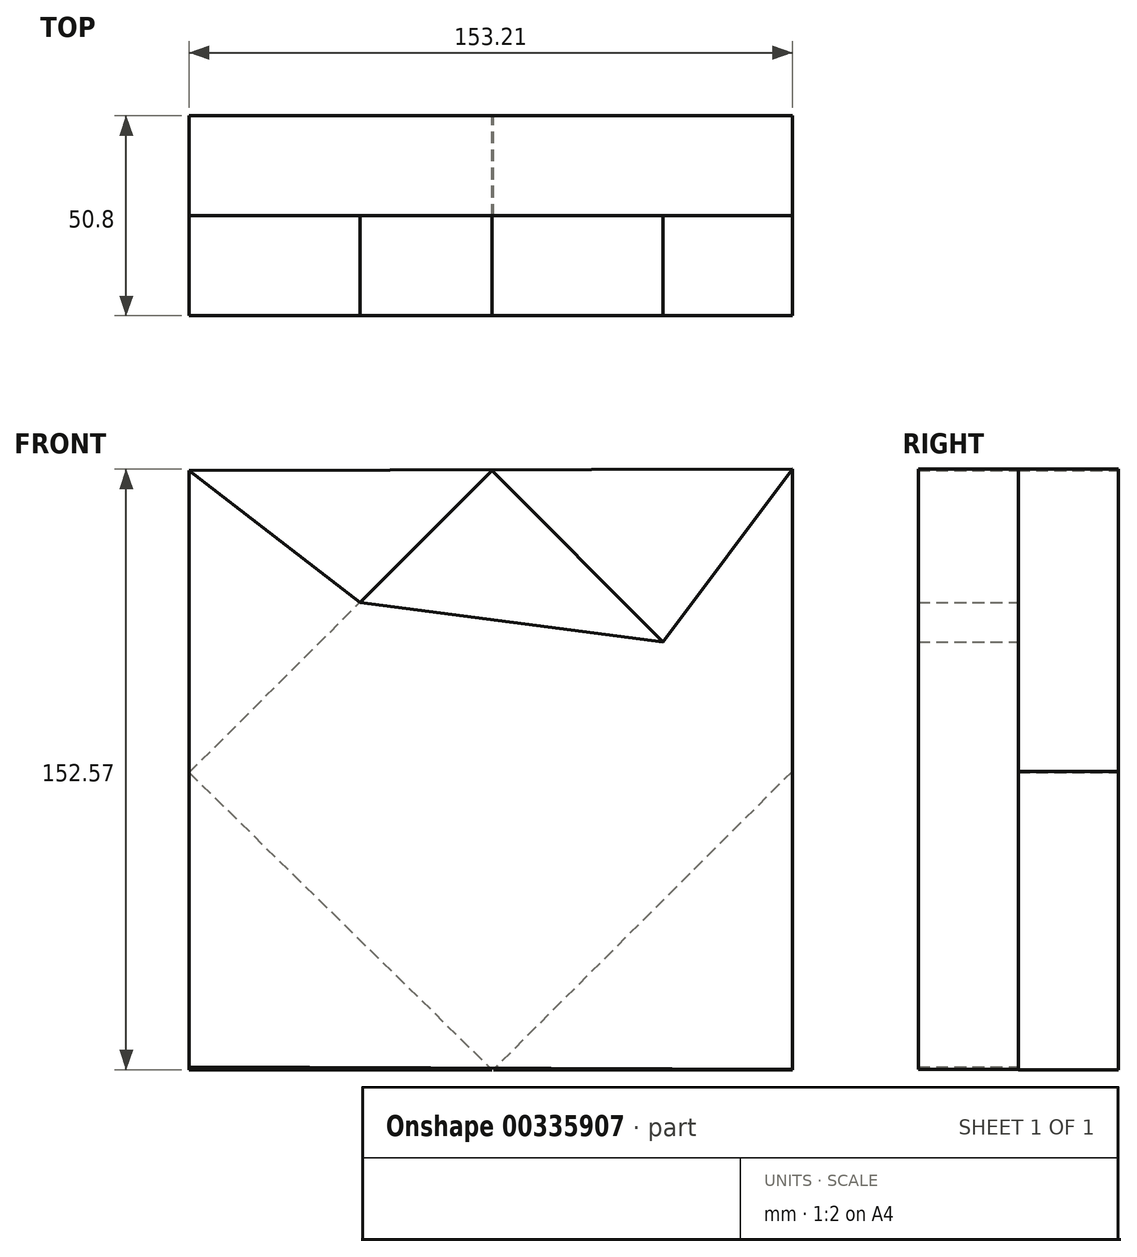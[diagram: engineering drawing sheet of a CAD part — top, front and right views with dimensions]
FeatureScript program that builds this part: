
annotation { "Feature Type Name" : "Feature", "Feature Type Description" : "" }
export const myFeature = defineFeature(function(context is Context, id is Id, definition is map)
    precondition{}
    {
        {
            var Q0;
            Q0=qCreatedBy(makeId("Front.planeOp"),FACE);
            var sketch = newSketch(context, id + "F0", { "sketchPlane" : qUnion([Q0])});
            skLineSegment(sketch, "E0", {"start": v(-76.93, 76.77) * mm, "end": v(-76.93, -75.47) * mm});
            skLineSegment(sketch, "E1", {"start": v(0, 0) * mm, "end": v(-76.93, 0) * mm});
            skLineSegment(sketch, "E2", {"start": v(0, 76.77) * mm, "end": v(0, 0) * mm});
            skLineSegment(sketch, "E3", {"start": v(0, 0) * mm, "end": v(0, -75.47) * mm});
            skLineSegment(sketch, "E4", {"start": v(0, -75.47) * mm, "end": v(-76.93, -75.47) * mm});
            skLineSegment(sketch, "E5", {"start": v(0, -75.47) * mm, "end": v(77.58, -75.47) * mm});
            skLineSegment(sketch, "E6", {"start": v(76.28, 77.1) * mm, "end": v(76.28, -75.47) * mm});
            skLineSegment(sketch, "E7", {"start": v(76.28, -75.47) * mm, "end": v(76.28, 77.1) * mm});
            skLineSegment(sketch, "E8", {"start": v(0, 76.77) * mm, "end": v(-76.93, 0) * mm});
            skLineSegment(sketch, "E9", {"start": v(0, 76.77) * mm, "end": v(76.28, 0.33) * mm});
            skLineSegment(sketch, "E10", {"start": v(76.28, 0.33) * mm, "end": v(0, -75.8) * mm});
            skLineSegment(sketch, "E11", {"start": v(-76.93, 0) * mm, "end": v(0, -75.47) * mm});
            skLineSegment(sketch, "E12", {"start": v(76.28, 0.33) * mm, "end": v(0, 0) * mm});
            skLineSegment(sketch, "E13", {"start": v(-76.93, 76.77) * mm, "end": v(76.28, 77.1) * mm});
            skSolve(sketch);
        }
        {
            var Q0;
            {var subQ3=sQuery(id+"F0.wireOp",EDGE,"E8");Q0=makeQuery(id+"F0.imprint","IMPRINT",FACE,{"disambiguationData":[TD([[makeQuery(id+"F0.imprint","IMPRINT",EDGE,{"derivedFrom":subQ3}),-1.0]])]});}
            var Q1;
            {var subQ0=sQuery(id+"F0.wireOp",EDGE,"E7");var subQ1=sQuery(id+"F0.wireOp",EDGE,"E5");var subQ2=makeQuery(id+"F0.imprint","INTERSECT",VERTEX,{"derivedFrom":[subQ1,subQ0]});Q1=makeQuery(id+"F0.imprint","IMPRINT",FACE,{"disambiguationData":[TD([[makeQuery(id+"F0.imprint","IMPRINT",EDGE,{"disambiguationData":[TD([[subQ2,1.0]])],"derivedFrom":subQ1}),1.0]])]});}
            var Q2;
            {var subQ0=sQuery(id+"F0.wireOp",EDGE,"E4");Q2=makeQuery(id+"F0.imprint","IMPRINT",FACE,{"disambiguationData":[TD([[makeQuery(id+"F0.imprint","IMPRINT",EDGE,{"derivedFrom":subQ0}),-1.0]])]});}
            extrude(context, id + "F1", {"entities" : qUnion([Q0, Q1, Q2]), "depth" : 25.4 * mm});
        }
        {
            var Q0;
            Q0=makeQuery(id+"F1.opExtrude","CAP_FACE",FACE,{"disambiguationData":[OSD([sQuery(id+"F0.wireOp",EDGE,"E0"),sQuery(id+"F0.wireOp",EDGE,"E7"),sQuery(id+"F0.wireOp",EDGE,"E8"),sQuery(id+"F0.wireOp",EDGE,"E9"),sQuery(id+"F0.wireOp",EDGE,"E13")])],"isStart":false});
            var sketch = newSketch(context, id + "F2", { "sketchPlane" : qUnion([Q0])});
            skLineSegment(sketch, "E14", {"start": v(-76.93, 76.77) * mm, "end": v(-33.56, 43.29) * mm});
            skLineSegment(sketch, "E15", {"start": v(76.28, 77.1) * mm, "end": v(43.42, 33.25) * mm});
            skLineSegment(sketch, "E16", {"start": v(76.28, -75.38) * mm, "end": v(30.01, -46.03) * mm});
            skLineSegment(sketch, "E17", {"start": v(-76.93, -74.78) * mm, "end": v(-30.27, -46.03) * mm});
            skLineSegment(sketch, "E18", {"start": v(-30.27, -46.03) * mm, "end": v(-33.56, 43.29) * mm});
            skLineSegment(sketch, "E19", {"start": v(43.42, 33.25) * mm, "end": v(-33.56, 43.29) * mm});
            skLineSegment(sketch, "E20", {"start": v(30.01, -46.03) * mm, "end": v(43.42, 33.25) * mm});
            skLineSegment(sketch, "E21", {"start": v(30.01, -46.03) * mm, "end": v(-30.27, -46.03) * mm});
            skLineSegment(sketch, "E22", {"start": v(76.28, 77.1) * mm, "end": v(76.28, -75.38) * mm});
            skLineSegment(sketch, "E23", {"start": v(76.28, -75.38) * mm, "end": v(-76.93, -74.78) * mm});
            skLineSegment(sketch, "E24", {"start": v(-76.93, -74.78) * mm, "end": v(-76.93, 76.77) * mm});
            skSolve(sketch);
        }
        {
            var Q0;
            {var subQ0=sQuery(id+"F2.wireOp",EDGE,"E19");Q0=makeQuery(id+"F2.imprint","IMPRINT",FACE,{"disambiguationData":[TD([[makeQuery(id+"F2.imprint","IMPRINT",EDGE,{"derivedFrom":subQ0}),-1.0]])]});}
            extrude(context, id + "F3", {"entities" : qUnion([Q0]), "depth" : 25.4 * mm});
        }
        {
            var Q0;
            Q0 = qSketchRegion(id + "F2", true);
            extrude(context, id + "F4", {"entities" : qUnion([Q0]), "depth" : 25.4 * mm});
        }
    });
